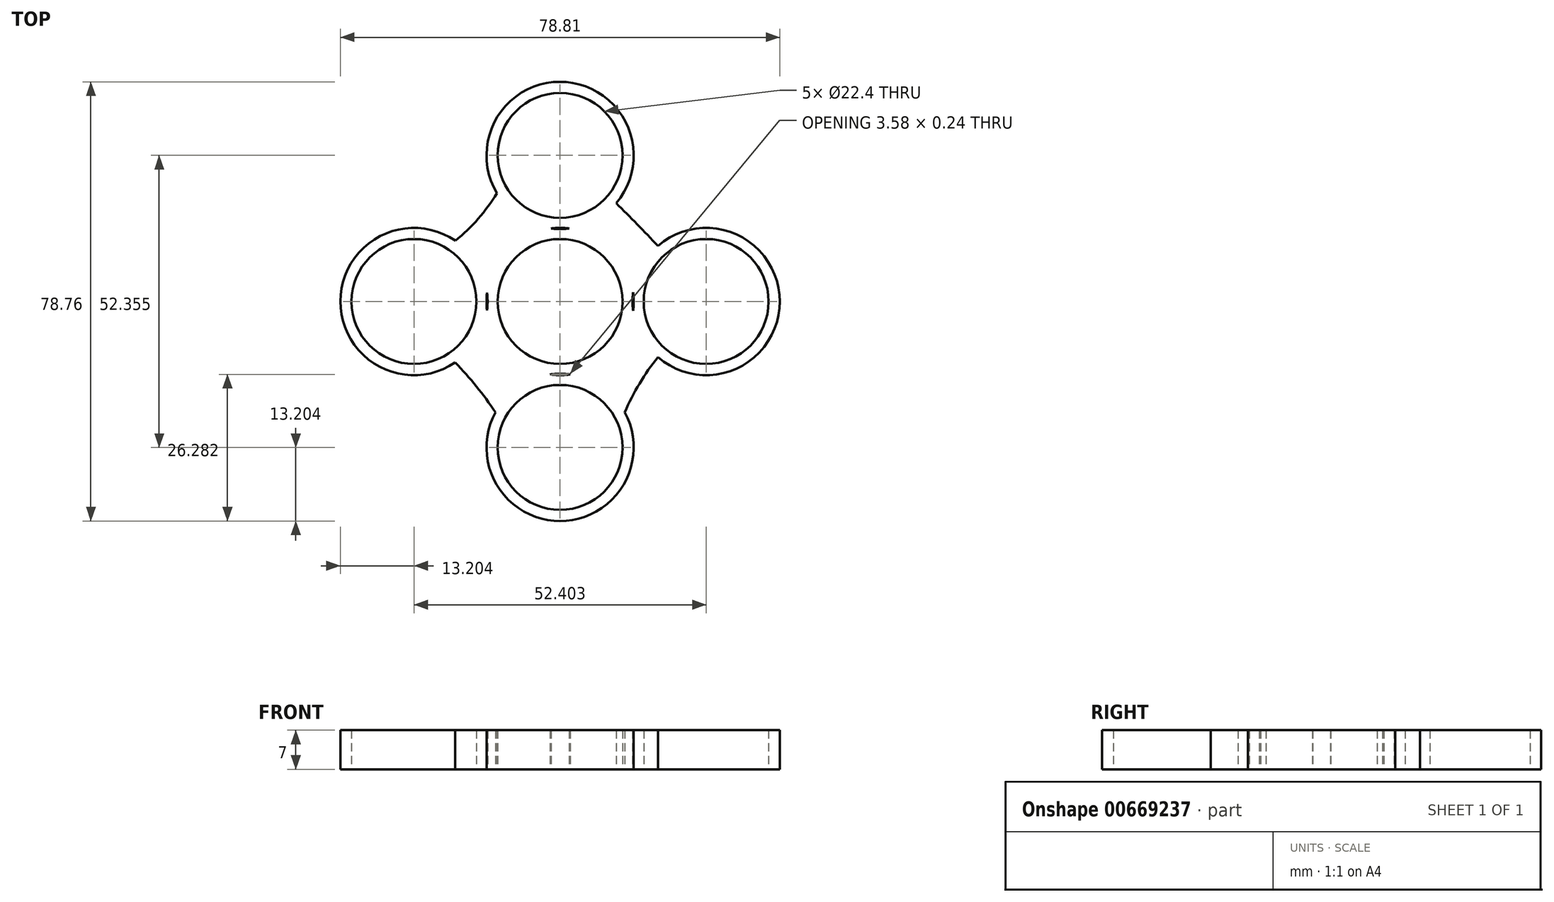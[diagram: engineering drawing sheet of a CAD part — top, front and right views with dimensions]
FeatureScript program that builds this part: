
annotation { "Feature Type Name" : "Feature", "Feature Type Description" : "" }
export const myFeature = defineFeature(function(context is Context, id is Id, definition is map)
    precondition{}
    {
        {
            var Q0;
            Q0=qCreatedBy(makeId("Top.planeOp"),FACE);
            var sketch = newSketch(context, id + "F0", { "sketchPlane" : qUnion([Q0])});
            skCircle(sketch, "E0", {"center": v(0, 0) * mm, "radius": 11.2 * mm});
            skCircle(sketch, "E1", {"center": v(0, 0) * mm, "radius": 13.2 * mm});
            skCircle(sketch, "E2", {"center": v(-26.2, 0) * mm, "radius": 11.2 * mm});
            skCircle(sketch, "E3", {"center": v(-26.2, 0) * mm, "radius": 13.2 * mm});
            skCircle(sketch, "E4", {"center": v(26.2, 0) * mm, "radius": 11.2 * mm});
            skCircle(sketch, "E5", {"center": v(26.2, 0) * mm, "radius": 13.2 * mm});
            skCircle(sketch, "E6", {"center": v(0, 26.2) * mm, "radius": 11.2 * mm});
            skCircle(sketch, "E7", {"center": v(0, 26.2) * mm, "radius": 13.2 * mm});
            skCircle(sketch, "E8", {"center": v(0, -26.16) * mm, "radius": 11.2 * mm});
            skCircle(sketch, "E9", {"center": v(0, -26.16) * mm, "radius": 13.2 * mm});
            skArc(sketch, "E10", {"start": v(17.54, 9.96) * mm, "mid": v(13.83, 13.84) * mm, "end": v(10.04, 17.63) * mm});
            skArc(sketch, "E11", {"start": v(-18.77, 10.9) * mm, "mid": v(-14.68, 14.84) * mm, "end": v(-11.33, 19.42) * mm});
            skArc(sketch, "E12", {"start": v(-11.6, -19.85) * mm, "mid": v(-15, -15.22) * mm, "end": v(-18.82, -10.94) * mm});
            skArc(sketch, "E13", {"start": v(17.54, -9.96) * mm, "mid": v(14.25, -14.71) * mm, "end": v(11.6, -19.85) * mm});
            skSolve(sketch);
        }
        {
            var Q0;
            {var subQ5=sQuery(id+"F0.wireOp",EDGE,"E10");Q0=makeQuery(id+"F0.imprint","IMPRINT",FACE,{"disambiguationData":[TD([[makeQuery(id+"F0.imprint","IMPRINT",EDGE,{"derivedFrom":subQ5}),1.0]])]});}
            var Q1;
            Q1=makeQuery(id+"F0.imprint","IMPRINT",FACE,{"disambiguationData":[TD([[makeQuery(id+"F0.imprint","IMPRINT",EDGE,{"derivedFrom":sQuery(id+"F0.wireOp",EDGE,"E4")}),-1.0]])]});
            var Q2;
            Q2=makeQuery(id+"F0.imprint","IMPRINT",FACE,{"disambiguationData":[TD([[makeQuery(id+"F0.imprint","IMPRINT",EDGE,{"derivedFrom":sQuery(id+"F0.wireOp",EDGE,"E6")}),-1.0]])]});
            var Q3;
            {var subQ5=sQuery(id+"F0.wireOp",EDGE,"E11");Q3=makeQuery(id+"F0.imprint","IMPRINT",FACE,{"disambiguationData":[TD([[makeQuery(id+"F0.imprint","IMPRINT",EDGE,{"derivedFrom":subQ5}),-1.0]])]});}
            var Q4;
            Q4=makeQuery(id+"F0.imprint","IMPRINT",FACE,{"disambiguationData":[TD([[makeQuery(id+"F0.imprint","IMPRINT",EDGE,{"derivedFrom":sQuery(id+"F0.wireOp",EDGE,"E2")}),-1.0]])]});
            var Q5;
            Q5=makeQuery(id+"F0.imprint","IMPRINT",FACE,{"disambiguationData":[TD([[makeQuery(id+"F0.imprint","IMPRINT",EDGE,{"derivedFrom":sQuery(id+"F0.wireOp",EDGE,"E0")}),-1.0]])]});
            var Q6;
            {var subQ5=sQuery(id+"F0.wireOp",EDGE,"E12");Q6=makeQuery(id+"F0.imprint","IMPRINT",FACE,{"disambiguationData":[TD([[makeQuery(id+"F0.imprint","IMPRINT",EDGE,{"derivedFrom":subQ5}),-1.0]])]});}
            var Q7;
            Q7=makeQuery(id+"F0.imprint","IMPRINT",FACE,{"disambiguationData":[TD([[makeQuery(id+"F0.imprint","IMPRINT",EDGE,{"derivedFrom":sQuery(id+"F0.wireOp",EDGE,"E8")}),-1.0]])]});
            var Q8;
            {var subQ5=sQuery(id+"F0.wireOp",EDGE,"E13");Q8=makeQuery(id+"F0.imprint","IMPRINT",FACE,{"disambiguationData":[TD([[makeQuery(id+"F0.imprint","IMPRINT",EDGE,{"derivedFrom":subQ5}),-1.0]])]});}
            extrude(context, id + "F1", {"entities" : qUnion([Q0, Q1, Q2, Q3, Q4, Q5, Q6, Q7, Q8]), "depth" : 7 * mm, "offsetDistance" : 25 * mm});
        }
    });
